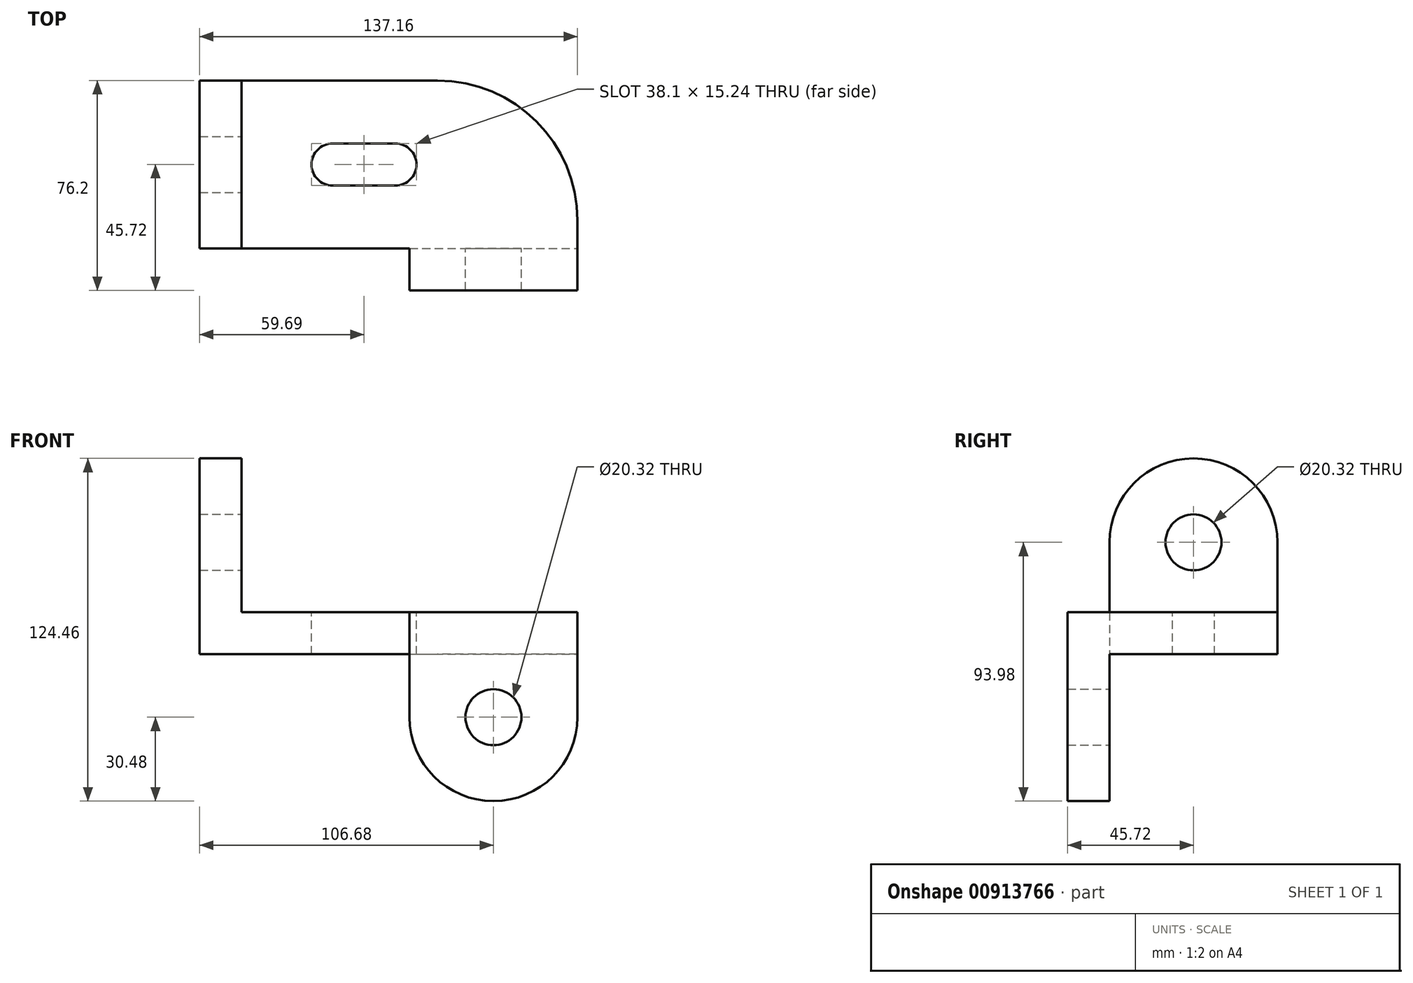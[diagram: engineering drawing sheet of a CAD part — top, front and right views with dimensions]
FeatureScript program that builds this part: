
annotation { "Feature Type Name" : "Feature", "Feature Type Description" : "" }
export const myFeature = defineFeature(function(context is Context, id is Id, definition is map)
    precondition{}
    {
        {
            var Q0;
            Q0=qCreatedBy(makeId("Top.planeOp"),FACE);
            var sketch = newSketch(context, id + "F0", { "sketchPlane" : qUnion([Q0])});
            skLineSegment(sketch, "E0.bottom", {"start": v(-68.58, 30.48) * mm, "end": v(68.58, 30.48) * mm});
            skLineSegment(sketch, "E0.top", {"start": v(-68.58, -30.48) * mm, "end": v(68.58, -30.48) * mm});
            skLineSegment(sketch, "E0.left", {"start": v(-68.58, 30.48) * mm, "end": v(-68.58, -30.48) * mm});
            skLineSegment(sketch, "E0.right", {"start": v(68.58, 30.48) * mm, "end": v(68.58, -30.48) * mm});
            skPoint(sketch, "E0.middle", {"position": v(0, 0) * mm});
            skLineSegment(sketch, "E1.bottom", {"start": v(-68.58, 30.48) * mm, "end": v(-53.34, 30.48) * mm});
            skLineSegment(sketch, "E1.top", {"start": v(-68.58, -30.48) * mm, "end": v(-53.34, -30.48) * mm});
            skLineSegment(sketch, "E1.right", {"start": v(-53.34, 30.48) * mm, "end": v(-53.34, -30.48) * mm});
            skSolve(sketch);
        }
        {
            var Q0;
            {var subQ3=sQuery(id+"F0.wireOp",EDGE,"E0.left");var subQ7=sQuery(id+"F0.wireOp",EDGE,"E0.right");Q0=qUnion([makeQuery(id+"F0.imprint","IMPRINT",FACE,{"disambiguationData":[TD([[makeQuery(id+"F0.imprint","IMPRINT",EDGE,{"derivedFrom":subQ7}),-1.0]])]}),makeQuery(id+"F0.imprint","IMPRINT",FACE,{"disambiguationData":[TD([[makeQuery(id+"F0.imprint","IMPRINT",EDGE,{"derivedFrom":subQ3}),1.0]])]})]);}
            extrude(context, id + "F1", {"entities" : qUnion([Q0]), "oppositeDirection" : true, "depth" : 15.24 * mm, "offsetDistance" : 25.4 * mm});
        }
        {
            var Q0;
            {var subQ2=sQuery(id+"F0.wireOp",EDGE,"E0.left");Q0=makeQuery(id+"F0.imprint","IMPRINT",FACE,{"disambiguationData":[TD([[makeQuery(id+"F0.imprint","IMPRINT",EDGE,{"derivedFrom":subQ2}),1.0]])]});}
            extrude(context, id + "F2", {"entities" : qUnion([Q0]), "operationType" : NewBodyOperationType.ADD, "depth" : 25.4 * mm, "offsetDistance" : 25.4 * mm});
        }
        {
            var Q0;
            Q0=makeQuery(id+"F2.opExtrude","SWEPT_FACE",FACE,{"disambiguationData":[OSD([sQuery(id+"F0.wireOp",EDGE,"E1.right")])]});
            var sketch = newSketch(context, id + "F3", { "sketchPlane" : qUnion([Q0])});
            skArc(sketch, "E2", {"start": v(30.48, 25.4) * mm, "mid": v(0, 55.88) * mm, "end": v(-30.48, 25.4) * mm});
            skCircle(sketch, "E3", {"center": v(0, 25.4) * mm, "radius": 10.16 * mm});
            skSolve(sketch);
        }
        {
            var Q0;
            Q0=makeQuery(id+"F3.imprint","IMPRINT",FACE,{"disambiguationData":[TD([[makeQuery(id+"F3.imprint","IMPRINT",EDGE,{"derivedFrom":sQuery(id+"F3.wireOp",EDGE,"E2")}),1.0]])]});
            extrude(context, id + "F4", {"entities" : qUnion([Q0]), "operationType" : NewBodyOperationType.ADD, "oppositeDirection" : true, "depth" : 15.24 * mm, "offsetDistance" : 25.4 * mm});
        }
        {
            var Q0;
            {var subQ0=sQuery(id+"F3.wireOp",EDGE,"E3");var subQ1=makeQuery(id+"F2.opExtrude","CAP_EDGE",EDGE,{"disambiguationData":[OSD([sQuery(id+"F0.wireOp",EDGE,"E1.right")])],"isStart":false});var subQ2=makeQuery(id+"F3.imprint","INTERSECT",VERTEX,{"disambiguationData":[OD(0.0)],"derivedFrom":[subQ1,subQ0]});Q0=makeQuery(id+"F3.imprint","IMPRINT",FACE,{"disambiguationData":[TD([[makeQuery(id+"F3.imprint","IMPRINT",EDGE,{"disambiguationData":[TD([[subQ2,1.0]])],"derivedFrom":subQ0}),1.0]])]});}
            var Q1;
            {var subQ0=sQuery(id+"F3.wireOp",EDGE,"E3");var subQ1=makeQuery(id+"F2.opExtrude","CAP_EDGE",EDGE,{"disambiguationData":[OSD([sQuery(id+"F0.wireOp",EDGE,"E1.right")])],"isStart":false});var subQ2=makeQuery(id+"F3.imprint","INTERSECT",VERTEX,{"disambiguationData":[OD(0.0)],"derivedFrom":[subQ1,subQ0]});Q1=makeQuery(id+"F3.imprint","IMPRINT",FACE,{"disambiguationData":[TD([[makeQuery(id+"F3.imprint","IMPRINT",EDGE,{"disambiguationData":[TD([[subQ2,-1.0]])],"derivedFrom":subQ0}),1.0]])]});}
            extrude(context, id + "F5", {"entities" : qUnion([Q0, Q1]), "operationType" : NewBodyOperationType.REMOVE, "endBound" : BoundingType.THROUGH_ALL, "oppositeDirection" : true, "depth" : 25.4 * mm, "offsetDistance" : 25.4 * mm});
        }
        {
            var Q0;
            {var subQ0=sQuery(id+"F0.wireOp",EDGE,"E0.top");Q0=makeQuery(id+"F2.boolean.opBoolean","MERGE",FACE,{"derivedFrom":[makeQuery(id+"F1.opExtrude","SWEPT_FACE",FACE,{"disambiguationData":[OSD([subQ0])]}),makeQuery(id+"F2.opExtrude","SWEPT_FACE",FACE,{"disambiguationData":[OSD([subQ0])]})]});}
            var sketch = newSketch(context, id + "F6", { "sketchPlane" : qUnion([Q0])});
            skLineSegment(sketch, "E4.bottom", {"start": v(68.58, 0) * mm, "end": v(7.62, 0) * mm});
            skLineSegment(sketch, "E4.top", {"start": v(68.58, -38.1) * mm, "end": v(7.62, -38.1) * mm});
            skLineSegment(sketch, "E4.left", {"start": v(68.58, 0) * mm, "end": v(68.58, -38.1) * mm});
            skLineSegment(sketch, "E4.right", {"start": v(7.62, 0) * mm, "end": v(7.62, -38.1) * mm});
            skArc(sketch, "E5", {"start": v(7.62, -38.1) * mm, "mid": v(38.1, -68.58) * mm, "end": v(68.58, -38.1) * mm});
            skCircle(sketch, "E6", {"center": v(38.1, -38.1) * mm, "radius": 10.16 * mm});
            skSolve(sketch);
        }
        {
            var Q0;
            {var subQ0=sQuery(id+"F6.wireOp",EDGE,"E4.bottom");Q0=makeQuery(id+"F6.imprint","IMPRINT",FACE,{"disambiguationData":[TD([[makeQuery(id+"F6.imprint","IMPRINT",EDGE,{"derivedFrom":subQ0}),-1.0]])]});}
            var Q1;
            {var subQ2=sQuery(id+"F6.wireOp",EDGE,"E4.top");var subQ9=sQuery(id+"F6.wireOp",EDGE,"E6");var subQ11=makeQuery(id+"F6.imprint","INTERSECT",VERTEX,{"disambiguationData":[OD(0.0)],"derivedFrom":[subQ2,subQ9]});Q1=makeQuery(id+"F6.imprint","IMPRINT",FACE,{"disambiguationData":[TD([[makeQuery(id+"F6.imprint","IMPRINT",EDGE,{"disambiguationData":[TD([[subQ11,-1.0]])],"derivedFrom":subQ9}),-1.0]])]});}
            var Q2;
            {var subQ0=sQuery(id+"F6.wireOp",EDGE,"E5");Q2=makeQuery(id+"F6.imprint","IMPRINT",FACE,{"disambiguationData":[TD([[makeQuery(id+"F6.imprint","IMPRINT",EDGE,{"derivedFrom":subQ0}),1.0]])]});}
            extrude(context, id + "F7", {"entities" : qUnion([Q0, Q1, Q2]), "operationType" : NewBodyOperationType.ADD, "depth" : 15.24 * mm, "offsetDistance" : 25.4 * mm});
        }
        {
            var Q0;
            Q0=makeQuery(id+"F1.opExtrude","SWEPT_EDGE",EDGE,{"disambiguationData":[OSD([sQuery(id+"F0.wireOp",EDGE,"E0.bottom"),sQuery(id+"F0.wireOp",EDGE,"E0.right")])]});
            fillet(context, id + "F8", {"entities" : qUnion([Q0]), "radius" : 50.8 * mm, "tangentPropagation" : true, "allowEdgeOverflow" : false});
        }
        {
            var Q0;
            Q0=makeQuery(id+"F7.boolean.opBoolean","MERGE",FACE,{"derivedFrom":[makeQuery(id+"F1.opExtrude","CAP_FACE",FACE,{"disambiguationData":[OSD([sQuery(id+"F0.wireOp",EDGE,"E0.bottom"),sQuery(id+"F0.wireOp",EDGE,"E0.top"),sQuery(id+"F0.wireOp",EDGE,"E0.left"),sQuery(id+"F0.wireOp",EDGE,"E0.right")])],"isStart":true}),makeQuery(id+"F7.opExtrude","SWEPT_FACE",FACE,{"disambiguationData":[OSD([sQuery(id+"F6.wireOp",EDGE,"E4.bottom")])]})]});
            var sketch = newSketch(context, id + "F9", { "sketchPlane" : qUnion([Q0])});
            skLineSegment(sketch, "E7.bottom", {"start": v(2.54, -7.62) * mm, "end": v(-20.32, -7.62) * mm});
            skLineSegment(sketch, "E7.top", {"start": v(2.54, 7.62) * mm, "end": v(-20.32, 7.62) * mm});
            skLineSegment(sketch, "E7.left", {"start": v(2.54, -7.62) * mm, "end": v(2.54, 7.62) * mm});
            skLineSegment(sketch, "E7.right", {"start": v(-20.32, -7.62) * mm, "end": v(-20.32, 7.62) * mm});
            skPoint(sketch, "E7.middle", {"position": v(-8.9, 0) * mm});
            skArc(sketch, "E8", {"start": v(-20.32, 7.62) * mm, "mid": v(-27.94, 0) * mm, "end": v(-20.32, -7.62) * mm});
            skArc(sketch, "E9", {"start": v(2.54, -7.62) * mm, "mid": v(10.16, 0) * mm, "end": v(2.54, 7.62) * mm});
            skSolve(sketch);
        }
        {
            var Q0;
            Q0 = qSketchRegion(id + "F9", true);
            extrude(context, id + "F10", {"entities" : qUnion([Q0]), "operationType" : NewBodyOperationType.REMOVE, "endBound" : BoundingType.THROUGH_ALL, "oppositeDirection" : true, "depth" : 25.4 * mm, "offsetDistance" : 25.4 * mm});
        }
    });
